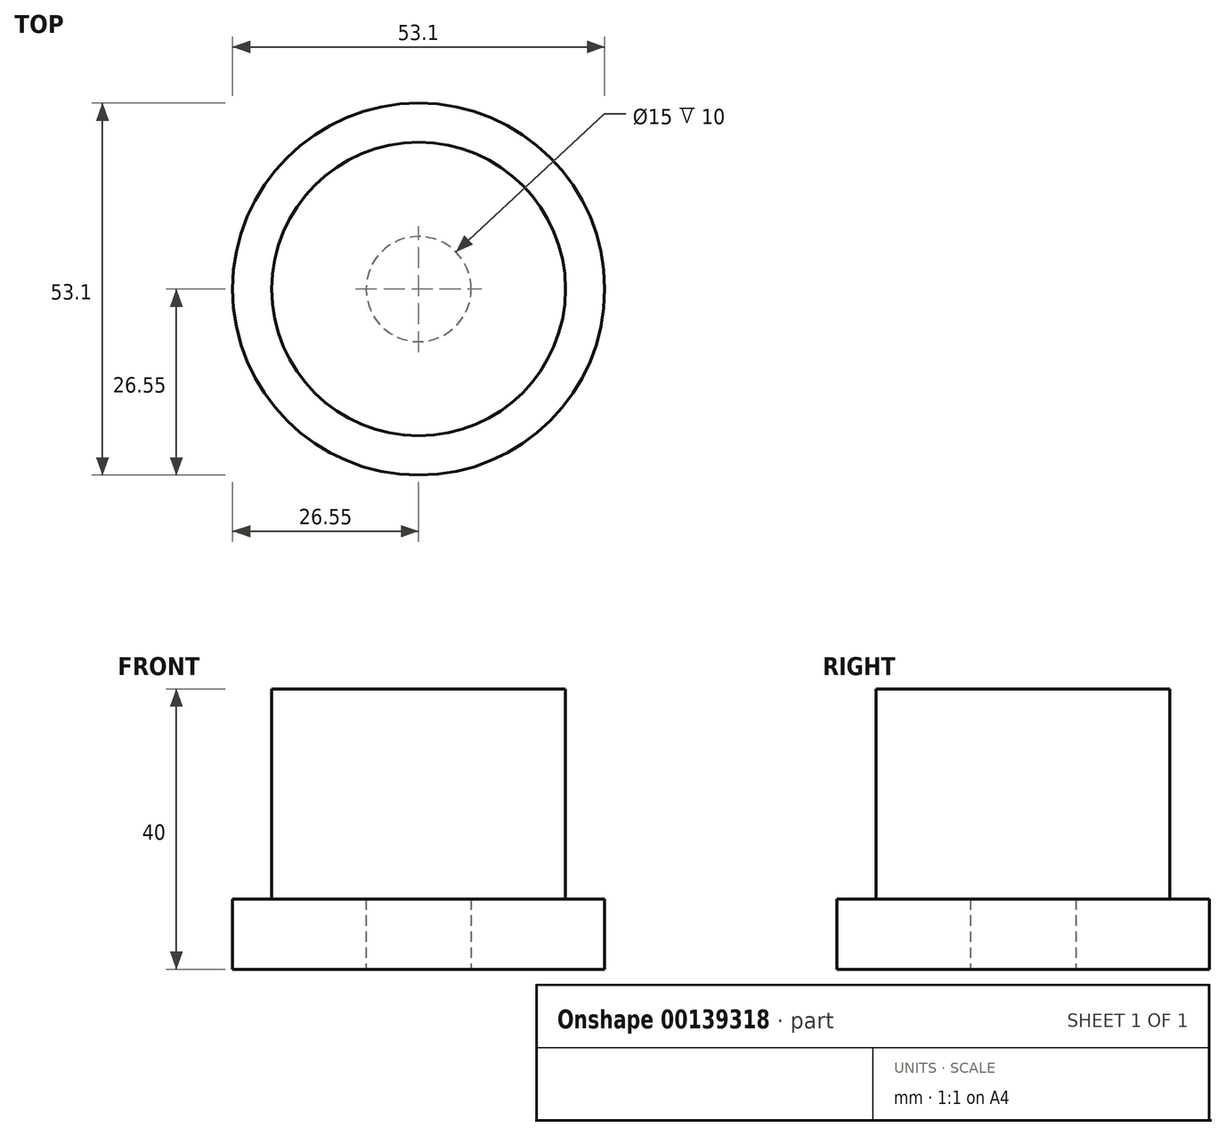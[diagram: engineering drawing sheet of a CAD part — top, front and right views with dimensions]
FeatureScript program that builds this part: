
annotation { "Feature Type Name" : "Feature", "Feature Type Description" : "" }
export const myFeature = defineFeature(function(context is Context, id is Id, definition is map)
    precondition{}
    {
        {
            var Q0;
            Q0=qCreatedBy(makeId("Top.planeOp"),FACE);
            var sketch = newSketch(context, id + "F0", { "sketchPlane" : qUnion([Q0])});
            skCircle(sketch, "E0", {"center": v(0, 0) * mm, "radius": 26.55 * mm});
            skCircle(sketch, "E1", {"center": v(0, 0) * mm, "radius": 7.5 * mm});
            skSolve(sketch);
        }
        {
            var Q0;
            Q0 = qSketchRegion(id + "F0", true);
            extrude(context, id + "F1", {"entities" : qUnion([Q0]), "depth" : 10 * mm});
        }
        {
            var Q0;
            Q0=makeQuery(id+"F1.opExtrude","CAP_FACE",FACE,{"disambiguationData":[OSD([sQuery(id+"F0.wireOp",EDGE,"E0"),sQuery(id+"F0.wireOp",EDGE,"E1")])],"isStart":false});
            var sketch = newSketch(context, id + "F2", { "sketchPlane" : qUnion([Q0])});
            skCircle(sketch, "E2", {"center": v(0, 0) * mm, "radius": 20.95 * mm});
            skSolve(sketch);
        }
        {
            var Q0;
            Q0 = qSketchRegion(id + "F2", true);
            extrude(context, id + "F3", {"entities" : qUnion([Q0]), "operationType" : NewBodyOperationType.ADD, "depth" : 30 * mm});
        }
    });
